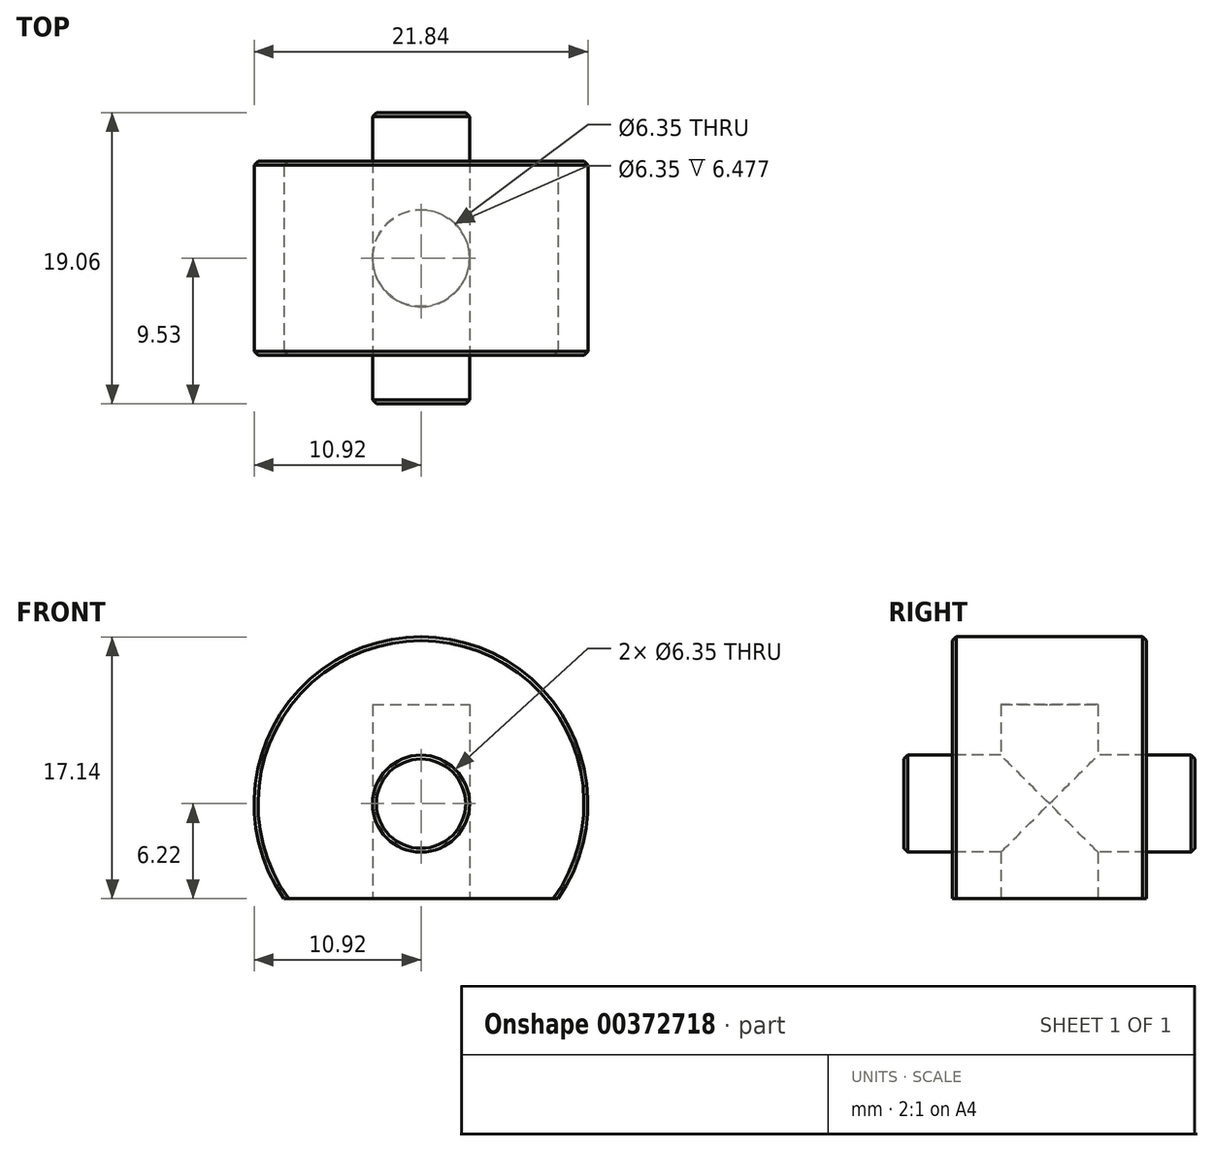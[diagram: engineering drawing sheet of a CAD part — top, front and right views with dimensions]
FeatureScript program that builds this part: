
annotation { "Feature Type Name" : "Feature", "Feature Type Description" : "" }
export const myFeature = defineFeature(function(context is Context, id is Id, definition is map)
    precondition{}
    {
        {
            var Q0;
            Q0=qCreatedBy(makeId("Right.planeOp"),FACE);
            var sketch = newSketch(context, id + "F0", { "sketchPlane" : qUnion([Q0])});
            skLineSegment(sketch, "E0.bottom", {"start": v(-9.52, 0) * mm, "end": v(9.53, 0) * mm});
            skLineSegment(sketch, "E0.top", {"start": v(-9.52, 3.17) * mm, "end": v(9.53, 3.17) * mm});
            skLineSegment(sketch, "E0.left", {"start": v(-9.52, 0) * mm, "end": v(-9.52, 3.17) * mm});
            skLineSegment(sketch, "E0.right", {"start": v(9.53, 0) * mm, "end": v(9.53, 3.17) * mm});
            skLineSegment(sketch, "E1.bottom", {"start": v(-6.35, 0) * mm, "end": v(6.35, 0) * mm});
            skLineSegment(sketch, "E1.top", {"start": v(-6.35, 10.92) * mm, "end": v(6.35, 10.92) * mm});
            skLineSegment(sketch, "E1.left", {"start": v(-6.35, 0) * mm, "end": v(-6.35, 10.92) * mm});
            skLineSegment(sketch, "E1.right", {"start": v(6.35, 0) * mm, "end": v(6.35, 10.92) * mm});
            skSolve(sketch);
        }
        {
            var Q0;
            {var subQ5=sQuery(id+"F0.wireOp",EDGE,"E1.top");Q0=makeQuery(id+"F0.imprint","IMPRINT",FACE,{"disambiguationData":[TD([[makeQuery(id+"F0.imprint","IMPRINT",EDGE,{"derivedFrom":subQ5}),-1.0]])]});}
            var Q1;
            {var subQ5=sQuery(id+"F0.wireOp",EDGE,"E1.bottom");Q1=makeQuery(id+"F0.imprint","IMPRINT",FACE,{"disambiguationData":[TD([[makeQuery(id+"F0.imprint","IMPRINT",EDGE,{"derivedFrom":subQ5}),1.0]])]});}
            var Q2;
            {var subQ0=sQuery(id+"F0.wireOp",EDGE,"E0.left");Q2=makeQuery(id+"F0.imprint","IMPRINT",FACE,{"disambiguationData":[TD([[makeQuery(id+"F0.imprint","IMPRINT",EDGE,{"derivedFrom":subQ0}),-1.0]])]});}
            var Q3;
            {var subQ0=sQuery(id+"F0.wireOp",EDGE,"E0.right");Q3=makeQuery(id+"F0.imprint","IMPRINT",FACE,{"disambiguationData":[TD([[makeQuery(id+"F0.imprint","IMPRINT",EDGE,{"derivedFrom":subQ0}),1.0]])]});}
            var Q4;
            Q4=sQuery(id+"F0.wireOp",EDGE,"E1.bottom");
            revolve(context, id + "F1", {"entities" : qUnion([Q0, Q1, Q2, Q3]), "axis" : qUnion([Q4]), "revolveType" : RevolveType.FULL});
        }
        {
            var Q0;
            Q0=makeQuery(id+"F1.opRevolve","SWEPT_FACE",FACE,{"disambiguationData":[OSD([sQuery(id+"F0.wireOp",EDGE,"E1.left")])]});
            var sketch = newSketch(context, id + "F2", { "sketchPlane" : qUnion([Q0])});
            skLineSegment(sketch, "E2.bottom", {"start": v(-10.87, -6.22) * mm, "end": v(15.66, -6.22) * mm});
            skLineSegment(sketch, "E2.top", {"start": v(-10.87, -16.04) * mm, "end": v(15.66, -16.04) * mm});
            skLineSegment(sketch, "E2.left", {"start": v(-10.87, -6.22) * mm, "end": v(-10.87, -16.04) * mm});
            skLineSegment(sketch, "E2.right", {"start": v(15.66, -6.22) * mm, "end": v(15.66, -16.04) * mm});
            skSolve(sketch);
        }
        {
            var Q0;
            Q0=makeQuery(id+"F2.imprint","IMPRINT",FACE,{"disambiguationData":[TD([[makeQuery(id+"F2.imprint","IMPRINT",EDGE,{"derivedFrom":sQuery(id+"F2.wireOp",EDGE,"E2.top")}),1.0]])]});
            var Q1;
            {var subQ0=sQuery(id+"F2.wireOp",EDGE,"E2.bottom");var subQ1=makeQuery(id+"F1.opRevolve","SWEPT_EDGE",EDGE,{"disambiguationData":[OSD([sQuery(id+"F0.wireOp",EDGE,"E1.top"),sQuery(id+"F0.wireOp",EDGE,"E1.left")])]});var subQ2=makeQuery(id+"F2.imprint","INTERSECT",VERTEX,{"disambiguationData":[OD(0.0)],"derivedFrom":[subQ1,subQ0]});Q1=makeQuery(id+"F2.imprint","IMPRINT",FACE,{"disambiguationData":[TD([[makeQuery(id+"F2.imprint","IMPRINT",EDGE,{"disambiguationData":[TD([[subQ2,-1.0]])],"derivedFrom":subQ0}),-1.0]])]});}
            extrude(context, id + "F3", {"entities" : qUnion([Q0, Q1]), "operationType" : NewBodyOperationType.REMOVE, "endBound" : BoundingType.THROUGH_ALL, "oppositeDirection" : true, "depth" : 25.4 * mm});
        }
        {
            var Q0;
            Q0=makeQuery(id+"F1.opRevolve","SWEPT_FACE",FACE,{"disambiguationData":[OSD([sQuery(id+"F0.wireOp",EDGE,"E0.left")])]});
            var Q1;
            Q1=makeQuery(id+"F1.opRevolve","SWEPT_EDGE",EDGE,{"disambiguationData":[OSD([sQuery(id+"F0.wireOp",EDGE,"E1.top"),sQuery(id+"F0.wireOp",EDGE,"E1.left")])]});
            var Q2;
            Q2=makeQuery(id+"F1.opRevolve","SWEPT_EDGE",EDGE,{"disambiguationData":[OSD([sQuery(id+"F0.wireOp",EDGE,"E1.top"),sQuery(id+"F0.wireOp",EDGE,"E1.right")])]});
            var Q3;
            Q3=makeQuery(id+"F1.opRevolve","SWEPT_EDGE",EDGE,{"disambiguationData":[OSD([sQuery(id+"F0.wireOp",EDGE,"E0.top"),sQuery(id+"F0.wireOp",EDGE,"E0.right")])]});
            chamfer(context, id + "F4", {"entities" : qUnion([Q0, Q1, Q2, Q3]), "width" : 0.25 * mm, "tangentPropagation" : true});
        }
        {
            var Q0;
            Q0=makeQuery(id+"F3.boolean.opBoolean","COPY",FACE,{"derivedFrom":makeQuery(id+"F3.opExtrude","SWEPT_FACE",FACE,{"disambiguationData":[OSD([sQuery(id+"F2.wireOp",EDGE,"E2.bottom")])]})});
            var sketch = newSketch(context, id + "F5", { "sketchPlane" : qUnion([Q0])});
            skCircle(sketch, "E3", {"center": v(0, 0) * mm, "radius": 3.18 * mm});
            skSolve(sketch);
        }
        {
            var Q0;
            Q0 = qSketchRegion(id + "F5", true);
            extrude(context, id + "F6", {"entities" : qUnion([Q0]), "operationType" : NewBodyOperationType.REMOVE, "oppositeDirection" : true, "depth" : 12.7 * mm});
        }
    });
